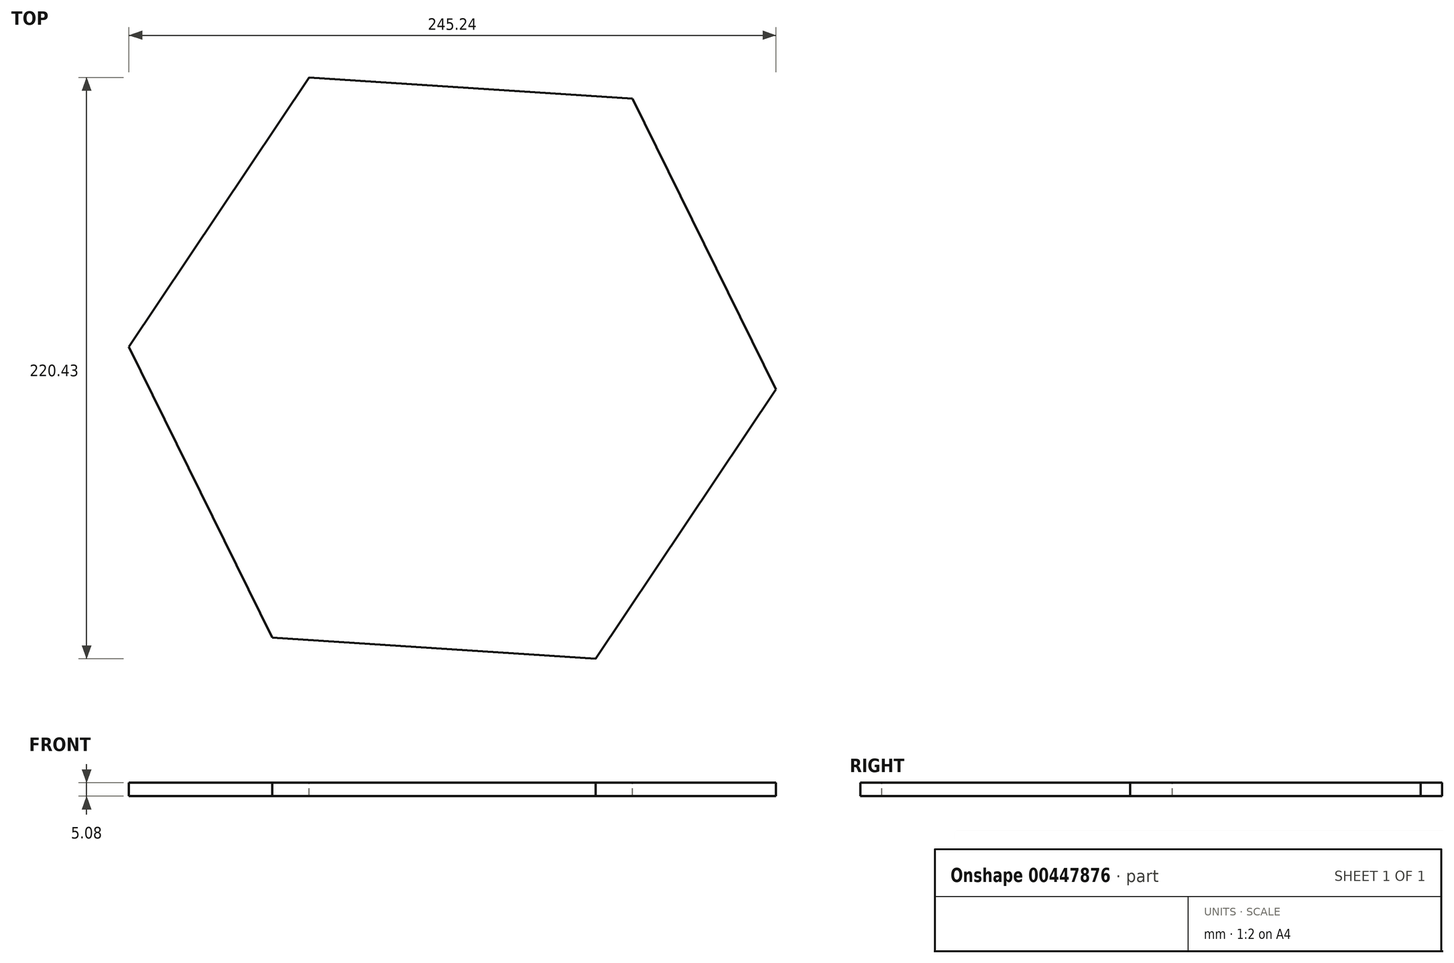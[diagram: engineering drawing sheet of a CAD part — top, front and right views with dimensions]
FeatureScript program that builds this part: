
annotation { "Feature Type Name" : "Feature", "Feature Type Description" : "" }
export const myFeature = defineFeature(function(context is Context, id is Id, definition is map)
    precondition{}
    {
        {
            var Q0;
            Q0=qCreatedBy(makeId("Top.planeOp"),FACE);
            var sketch = newSketch(context, id + "F0", { "sketchPlane" : qUnion([Q0])});
            skCircle(sketch, "E0.cCircle", {"center": v(-37.48, 91.27) * mm, "radius": 122.88 * mm, "construction": true});
            skLineSegment(sketch, "E0.0", {"start": v(-91.82, 201.48) * mm, "end": v(30.8, 193.43) * mm});
            skLineSegment(sketch, "E0.1", {"start": v(30.8, 193.43) * mm, "end": v(85.14, 83.2) * mm});
            skLineSegment(sketch, "E0.2", {"start": v(85.14, 83.2) * mm, "end": v(16.85, -18.95) * mm});
            skLineSegment(sketch, "E0.3", {"start": v(16.85, -18.95) * mm, "end": v(-105.77, -10.9) * mm});
            skLineSegment(sketch, "E0.4", {"start": v(-105.77, -10.9) * mm, "end": v(-160.1, 99.32) * mm});
            skLineSegment(sketch, "E0.5", {"start": v(-160.1, 99.32) * mm, "end": v(-91.82, 201.48) * mm});
            skSolve(sketch);
        }
        {
            var Q0;
            Q0 = qSketchRegion(id + "F0", true);
            var sketch = newSketch(context, id + "F1", { "sketchPlane" : qUnion([Q0])});
            skSolve(sketch);
        }
        {
            var Q0;
            Q0 = qSketchRegion(id + "F1", true);
            var Q1;
            Q1=makeQuery(id+"F0.imprint","IMPRINT",FACE,{"disambiguationData":[TD([[makeQuery(id+"F0.imprint","IMPRINT",EDGE,{"derivedFrom":sQuery(id+"F0.wireOp",EDGE,"E0.0")}),-1.0]])]});
            extrude(context, id + "F2", {"entities" : qUnion([Q0, Q1]), "oppositeDirection" : true, "depth" : 5.08 * mm});
        }
    });
